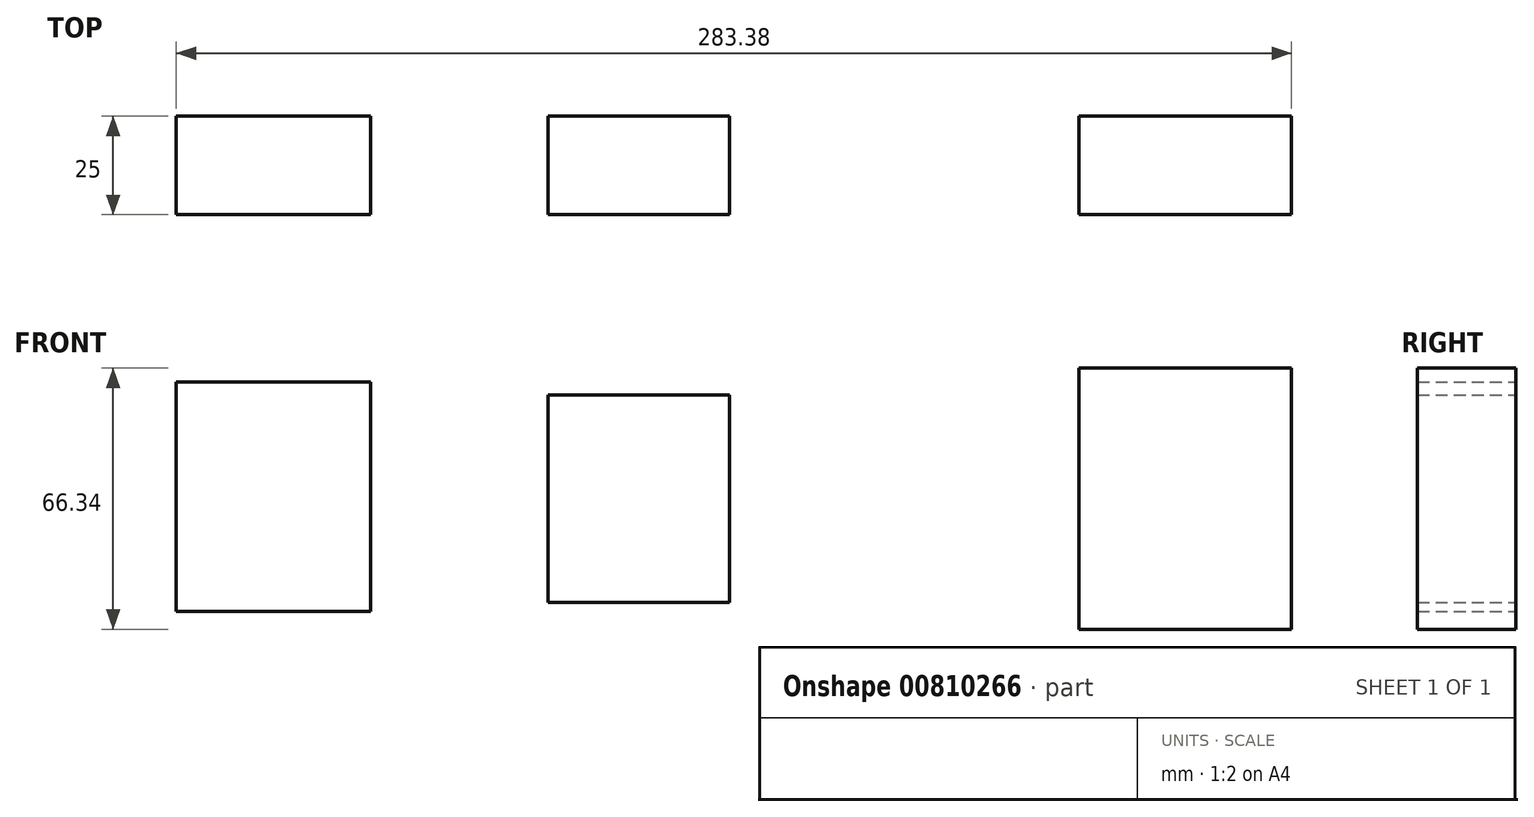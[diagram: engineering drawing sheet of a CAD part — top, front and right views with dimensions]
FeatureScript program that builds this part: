
annotation { "Feature Type Name" : "Feature", "Feature Type Description" : "" }
export const myFeature = defineFeature(function(context is Context, id is Id, definition is map)
    precondition{}
    {
        {
            var Q0;
            Q0=qCreatedBy(makeId("Front.planeOp"),FACE);
            var sketch = newSketch(context, id + "F0", { "sketchPlane" : qUnion([Q0])});
            skLineSegment(sketch, "E0.bottom", {"start": v(-141.2, 20.83) * mm, "end": v(-91.8, 20.83) * mm});
            skLineSegment(sketch, "E0.top", {"start": v(-141.2, 79.15) * mm, "end": v(-91.8, 79.15) * mm});
            skLineSegment(sketch, "E0.left", {"start": v(-141.2, 20.83) * mm, "end": v(-141.2, 79.15) * mm});
            skLineSegment(sketch, "E0.right", {"start": v(-91.8, 20.83) * mm, "end": v(-91.8, 79.15) * mm});
            skPoint(sketch, "E0.middle", {"position": v(-116.5, 49.99) * mm});
            skLineSegment(sketch, "E1.bottom", {"start": v(-46.73, 23.06) * mm, "end": v(-0.67, 23.06) * mm});
            skLineSegment(sketch, "E1.top", {"start": v(-46.73, 75.74) * mm, "end": v(-0.67, 75.74) * mm});
            skLineSegment(sketch, "E1.left", {"start": v(-46.73, 23.06) * mm, "end": v(-46.73, 75.74) * mm});
            skLineSegment(sketch, "E1.right", {"start": v(-0.67, 23.06) * mm, "end": v(-0.67, 75.74) * mm});
            skPoint(sketch, "E1.middle", {"position": v(-23.7, 49.4) * mm});
            skLineSegment(sketch, "E2.bottom", {"start": v(88.12, 16.26) * mm, "end": v(142.2, 16.26) * mm});
            skLineSegment(sketch, "E2.top", {"start": v(88.12, 82.6) * mm, "end": v(142.2, 82.6) * mm});
            skLineSegment(sketch, "E2.left", {"start": v(88.12, 16.26) * mm, "end": v(88.12, 82.6) * mm});
            skLineSegment(sketch, "E2.right", {"start": v(142.2, 16.26) * mm, "end": v(142.2, 82.6) * mm});
            skPoint(sketch, "E2.middle", {"position": v(115.16, 49.43) * mm});
            skSolve(sketch);
        }
        {
            var Q0;
            Q0=makeQuery(id+"F0.imprint","IMPRINT",FACE,{"disambiguationData":[TD([[makeQuery(id+"F0.imprint","IMPRINT",EDGE,{"derivedFrom":sQuery(id+"F0.wireOp",EDGE,"E0.bottom")}),1.0]])]});
            var Q1;
            Q1=makeQuery(id+"F0.imprint","IMPRINT",FACE,{"disambiguationData":[TD([[makeQuery(id+"F0.imprint","IMPRINT",EDGE,{"derivedFrom":sQuery(id+"F0.wireOp",EDGE,"E1.bottom")}),1.0]])]});
            var Q2;
            Q2=makeQuery(id+"F0.imprint","IMPRINT",FACE,{"disambiguationData":[TD([[makeQuery(id+"F0.imprint","IMPRINT",EDGE,{"derivedFrom":sQuery(id+"F0.wireOp",EDGE,"E2.bottom")}),1.0]])]});
            extrude(context, id + "F1", {"entities" : qUnion([Q0, Q1, Q2]), "depth" : 25 * mm, "offsetDistance" : 25 * mm});
        }
    });
